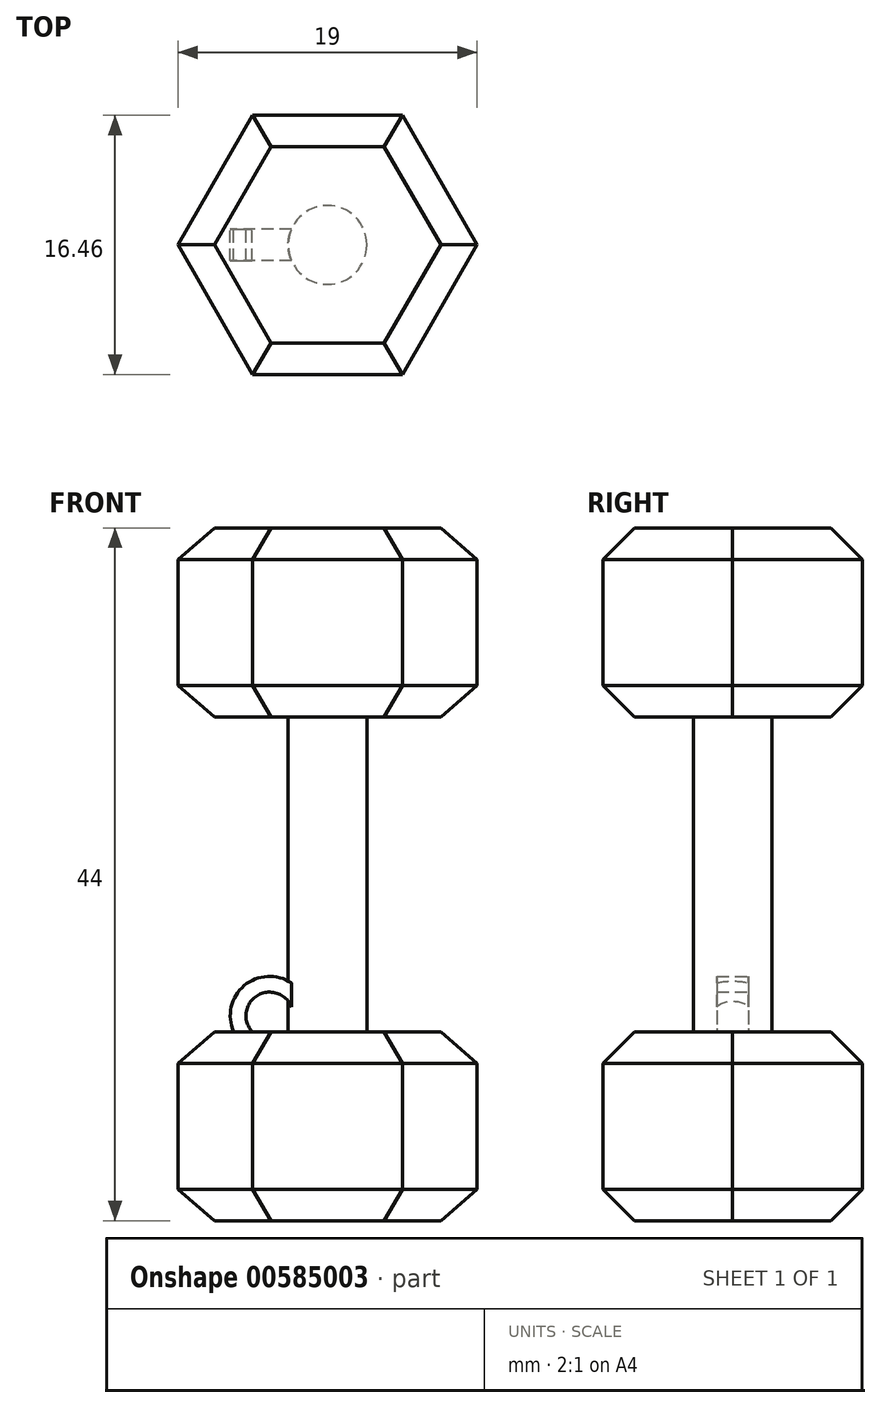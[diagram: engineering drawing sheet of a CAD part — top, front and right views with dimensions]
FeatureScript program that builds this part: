
annotation { "Feature Type Name" : "Feature", "Feature Type Description" : "" }
export const myFeature = defineFeature(function(context is Context, id is Id, definition is map)
    precondition{}
    {
        {
            var Q0;
            Q0=qCreatedBy(makeId("Top.planeOp"),FACE);
            var sketch = newSketch(context, id + "F0", { "sketchPlane" : qUnion([Q0])});
            skCircle(sketch, "E0.cCircle", {"center": v(0, 0) * mm, "radius": 9.5 * mm, "construction": true});
            skLineSegment(sketch, "E0.0", {"start": v(-4.75, -8.23) * mm, "end": v(-9.5, 0) * mm});
            skLineSegment(sketch, "E0.1", {"start": v(-9.5, 0) * mm, "end": v(-4.75, 8.23) * mm});
            skLineSegment(sketch, "E0.2", {"start": v(-4.75, 8.23) * mm, "end": v(4.75, 8.23) * mm});
            skLineSegment(sketch, "E0.3", {"start": v(4.75, 8.23) * mm, "end": v(9.5, 0) * mm});
            skLineSegment(sketch, "E0.4", {"start": v(9.5, 0) * mm, "end": v(4.75, -8.23) * mm});
            skLineSegment(sketch, "E0.5", {"start": v(4.75, -8.23) * mm, "end": v(-4.75, -8.23) * mm});
            skSolve(sketch);
        }
        {
            var Q0;
            Q0 = qSketchRegion(id + "F0", true);
            extrude(context, id + "F1", {"entities" : qUnion([Q0]), "depth" : 12 * mm, "offsetDistance" : 25 * mm});
        }
        {
            var Q0;
            Q0=makeQuery(id+"F1.opExtrude","CAP_FACE",FACE,{"disambiguationData":[OSD([sQuery(id+"F0.wireOp",EDGE,"E0.0"),sQuery(id+"F0.wireOp",EDGE,"E0.1"),sQuery(id+"F0.wireOp",EDGE,"E0.2"),sQuery(id+"F0.wireOp",EDGE,"E0.3"),sQuery(id+"F0.wireOp",EDGE,"E0.4"),sQuery(id+"F0.wireOp",EDGE,"E0.5")])],"isStart":true});
            var Q1;
            Q1=makeQuery(id+"F1.opExtrude","CAP_FACE",FACE,{"disambiguationData":[OSD([sQuery(id+"F0.wireOp",EDGE,"E0.0"),sQuery(id+"F0.wireOp",EDGE,"E0.1"),sQuery(id+"F0.wireOp",EDGE,"E0.2"),sQuery(id+"F0.wireOp",EDGE,"E0.3"),sQuery(id+"F0.wireOp",EDGE,"E0.4"),sQuery(id+"F0.wireOp",EDGE,"E0.5")])],"isStart":false});
            chamfer(context, id + "F2", {"entities" : qUnion([Q0, Q1]), "width" : 2 * mm, "tangentPropagation" : true});
        }
        {
            var Q0;
            Q0=makeQuery(id+"F1.opExtrude","CAP_FACE",FACE,{"disambiguationData":[OSD([sQuery(id+"F0.wireOp",EDGE,"E0.0"),sQuery(id+"F0.wireOp",EDGE,"E0.1"),sQuery(id+"F0.wireOp",EDGE,"E0.2"),sQuery(id+"F0.wireOp",EDGE,"E0.3"),sQuery(id+"F0.wireOp",EDGE,"E0.4"),sQuery(id+"F0.wireOp",EDGE,"E0.5")])],"isStart":false});
            var sketch = newSketch(context, id + "F3", { "sketchPlane" : qUnion([Q0])});
            skCircle(sketch, "E1", {"center": v(0, 0) * mm, "radius": 2.5 * mm});
            skSolve(sketch);
        }
        {
            var Q0;
            Q0 = qSketchRegion(id + "F3", true);
            extrude(context, id + "F4", {"entities" : qUnion([Q0]), "operationType" : NewBodyOperationType.ADD, "depth" : 10 * mm, "offsetDistance" : 25 * mm});
        }
        {
            var Q0;
            Q0=makeQuery(id+"F1.opExtrude","SWEPT_BODY",BODY,{"disambiguationData":[OSD([sQuery(id+"F0.wireOp",EDGE,"E0.0"),sQuery(id+"F0.wireOp",EDGE,"E0.1"),sQuery(id+"F0.wireOp",EDGE,"E0.2"),sQuery(id+"F0.wireOp",EDGE,"E0.3"),sQuery(id+"F0.wireOp",EDGE,"E0.4"),sQuery(id+"F0.wireOp",EDGE,"E0.5")])]});
            var Q1;
            Q1=makeQuery(id+"F4.opExtrude","CAP_FACE",FACE,{"disambiguationData":[OSD([sQuery(id+"F3.wireOp",EDGE,"E1")])],"isStart":false});
            mirror(context, id + "F5", {"operationType" : NewBodyOperationType.ADD, "entities" : qUnion([Q0]), "mirrorPlane" : qUnion([Q1])});
        }
        {
            var Q0;
            Q0=qCreatedBy(makeId("Front.planeOp"),FACE);
            var sketch = newSketch(context, id + "F6", { "sketchPlane" : qUnion([Q0])});
            skArc(sketch, "E2", {"start": v(-2.22, 15.05) * mm, "mid": v(-5.26, 14.95) * mm, "end": v(-5.96, 11.99) * mm});
            skArc(sketch, "E3", {"start": v(-2.22, 13.35) * mm, "mid": v(-4.39, 14.34) * mm, "end": v(-4.77, 11.99) * mm});
            skLineSegment(sketch, "E4", {"start": v(-5.96, 11.99) * mm, "end": v(-2.22, 11.99) * mm});
            skLineSegment(sketch, "E5", {"start": v(-2.22, 11.99) * mm, "end": v(-2.22, 15.05) * mm});
            skSolve(sketch);
        }
        {
            var Q0;
            {var subQ0=sQuery(id+"F6.wireOp",EDGE,"E2");Q0=makeQuery(id+"F6.imprint","IMPRINT",FACE,{"disambiguationData":[TD([[makeQuery(id+"F6.imprint","IMPRINT",EDGE,{"derivedFrom":subQ0}),1.0]])]});}
            extrude(context, id + "F7", {"entities" : qUnion([Q0]), "operationType" : NewBodyOperationType.ADD, "depth" : 1 * mm, "offsetDistance" : 25 * mm, "hasSecondDirection" : true, "secondDirectionOppositeDirection" : true, "secondDirectionDepth" : 1 * mm});
        }
    });
